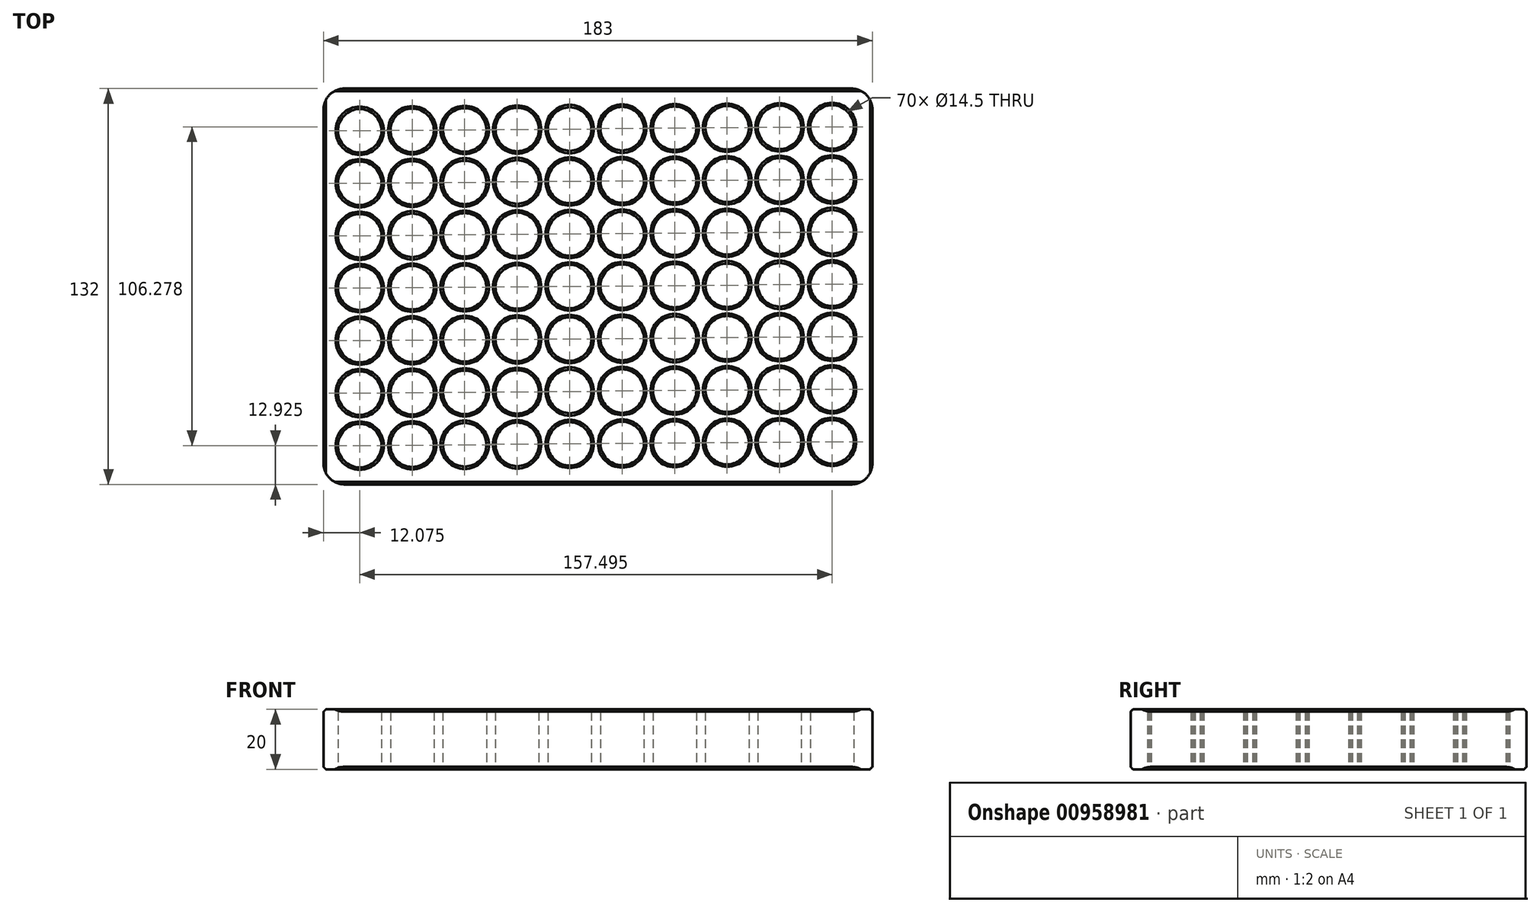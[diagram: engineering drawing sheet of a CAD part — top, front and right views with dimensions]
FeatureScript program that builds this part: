
annotation { "Feature Type Name" : "Feature", "Feature Type Description" : "" }
export const myFeature = defineFeature(function(context is Context, id is Id, definition is map)
    precondition{}
    {
        {
            var Q0;
            Q0=qCreatedBy(makeId("Top.planeOp"),FACE);
            var sketch = newSketch(context, id + "F0", { "sketchPlane" : qUnion([Q0])});
            skCircle(sketch, "E0", {"center": v(-65.97, 12.93) * mm, "radius": 7.25 * mm});
            skCircle(sketch, "E1.0.1.0", {"center": v(-65.97, 30.43) * mm, "radius": 7.25 * mm});
            skCircle(sketch, "E1.1.0.0", {"center": v(-48.47, 13.07) * mm, "radius": 7.25 * mm});
            skCircle(sketch, "E1.1.1.0", {"center": v(-48.47, 30.57) * mm, "radius": 7.25 * mm});
            skLineSegment(sketch, "E1.direction1", {"start": v(-65.97, 12.93) * mm, "end": v(-48.47, 13.07) * mm, "construction": true});
            skLineSegment(sketch, "E1.direction2", {"start": v(-65.97, 12.93) * mm, "end": v(-65.97, 30.43) * mm, "construction": true});
            skLineSegment(sketch, "E2.bottom", {"start": v(-78.04, 132) * mm, "end": v(104.96, 132) * mm});
            skLineSegment(sketch, "E2.top", {"start": v(-78.04, 0) * mm, "end": v(104.96, 0) * mm});
            skLineSegment(sketch, "E2.left", {"start": v(-78.04, 132) * mm, "end": v(-78.04, 0) * mm});
            skLineSegment(sketch, "E2.right", {"start": v(104.96, 132) * mm, "end": v(104.96, 0) * mm});
            skCircle(sketch, "E3.0.0.2", {"center": v(-65.97, 47.93) * mm, "radius": 7.25 * mm});
            skCircle(sketch, "E3.0.0.3", {"center": v(-65.97, 65.43) * mm, "radius": 7.25 * mm});
            skCircle(sketch, "E3.0.0.4", {"center": v(-65.97, 82.93) * mm, "radius": 7.25 * mm});
            skCircle(sketch, "E3.0.0.5", {"center": v(-65.97, 100.43) * mm, "radius": 7.25 * mm});
            skCircle(sketch, "E3.0.0.6", {"center": v(-65.97, 117.93) * mm, "radius": 7.25 * mm});
            skCircle(sketch, "E3.0.1.2", {"center": v(-48.47, 48.07) * mm, "radius": 7.25 * mm});
            skCircle(sketch, "E3.0.1.3", {"center": v(-48.47, 65.57) * mm, "radius": 7.25 * mm});
            skCircle(sketch, "E3.0.1.4", {"center": v(-48.47, 83.07) * mm, "radius": 7.25 * mm});
            skCircle(sketch, "E3.0.1.5", {"center": v(-48.47, 100.57) * mm, "radius": 7.25 * mm});
            skCircle(sketch, "E3.0.1.6", {"center": v(-48.47, 118.07) * mm, "radius": 7.25 * mm});
            skCircle(sketch, "E4.0.2.0", {"center": v(-30.97, 13.2) * mm, "radius": 7.25 * mm});
            skCircle(sketch, "E4.0.2.1", {"center": v(-30.97, 30.7) * mm, "radius": 7.25 * mm});
            skCircle(sketch, "E4.0.2.2", {"center": v(-30.97, 48.2) * mm, "radius": 7.25 * mm});
            skCircle(sketch, "E4.0.2.3", {"center": v(-30.97, 65.7) * mm, "radius": 7.25 * mm});
            skCircle(sketch, "E4.0.2.4", {"center": v(-30.97, 83.2) * mm, "radius": 7.25 * mm});
            skCircle(sketch, "E4.0.2.5", {"center": v(-30.97, 100.7) * mm, "radius": 7.25 * mm});
            skCircle(sketch, "E4.0.2.6", {"center": v(-30.97, 118.2) * mm, "radius": 7.25 * mm});
            skCircle(sketch, "E4.0.3.0", {"center": v(-13.47, 13.35) * mm, "radius": 7.25 * mm});
            skCircle(sketch, "E4.0.3.1", {"center": v(-13.47, 30.85) * mm, "radius": 7.25 * mm});
            skCircle(sketch, "E4.0.3.2", {"center": v(-13.47, 48.35) * mm, "radius": 7.25 * mm});
            skCircle(sketch, "E4.0.3.3", {"center": v(-13.47, 65.85) * mm, "radius": 7.25 * mm});
            skCircle(sketch, "E4.0.3.4", {"center": v(-13.47, 83.35) * mm, "radius": 7.25 * mm});
            skCircle(sketch, "E4.0.3.5", {"center": v(-13.47, 100.85) * mm, "radius": 7.25 * mm});
            skCircle(sketch, "E4.0.3.6", {"center": v(-13.47, 118.35) * mm, "radius": 7.25 * mm});
            skCircle(sketch, "E4.0.4.0", {"center": v(4.03, 13.5) * mm, "radius": 7.25 * mm});
            skCircle(sketch, "E4.0.4.1", {"center": v(4.03, 31) * mm, "radius": 7.25 * mm});
            skCircle(sketch, "E4.0.4.2", {"center": v(4.03, 48.5) * mm, "radius": 7.25 * mm});
            skCircle(sketch, "E4.0.4.3", {"center": v(4.03, 66) * mm, "radius": 7.25 * mm});
            skCircle(sketch, "E4.0.4.4", {"center": v(4.03, 83.5) * mm, "radius": 7.25 * mm});
            skCircle(sketch, "E4.0.4.5", {"center": v(4.03, 101) * mm, "radius": 7.25 * mm});
            skCircle(sketch, "E4.0.4.6", {"center": v(4.03, 118.5) * mm, "radius": 7.25 * mm});
            skCircle(sketch, "E4.0.5.0", {"center": v(21.53, 13.63) * mm, "radius": 7.25 * mm});
            skCircle(sketch, "E4.0.5.1", {"center": v(21.53, 31.13) * mm, "radius": 7.25 * mm});
            skCircle(sketch, "E4.0.5.2", {"center": v(21.53, 48.63) * mm, "radius": 7.25 * mm});
            skCircle(sketch, "E4.0.5.3", {"center": v(21.53, 66.13) * mm, "radius": 7.25 * mm});
            skCircle(sketch, "E4.0.5.4", {"center": v(21.53, 83.63) * mm, "radius": 7.25 * mm});
            skCircle(sketch, "E4.0.5.5", {"center": v(21.53, 101.13) * mm, "radius": 7.25 * mm});
            skCircle(sketch, "E4.0.5.6", {"center": v(21.53, 118.63) * mm, "radius": 7.25 * mm});
            skCircle(sketch, "E4.0.6.0", {"center": v(39.03, 13.78) * mm, "radius": 7.25 * mm});
            skCircle(sketch, "E4.0.6.1", {"center": v(39.03, 31.28) * mm, "radius": 7.25 * mm});
            skCircle(sketch, "E4.0.6.2", {"center": v(39.03, 48.78) * mm, "radius": 7.25 * mm});
            skCircle(sketch, "E4.0.6.3", {"center": v(39.03, 66.28) * mm, "radius": 7.25 * mm});
            skCircle(sketch, "E4.0.6.4", {"center": v(39.03, 83.78) * mm, "radius": 7.25 * mm});
            skCircle(sketch, "E4.0.6.5", {"center": v(39.03, 101.28) * mm, "radius": 7.25 * mm});
            skCircle(sketch, "E4.0.6.6", {"center": v(39.03, 118.78) * mm, "radius": 7.25 * mm});
            skCircle(sketch, "E4.0.7.0", {"center": v(56.53, 13.92) * mm, "radius": 7.25 * mm});
            skCircle(sketch, "E4.0.7.1", {"center": v(56.53, 31.42) * mm, "radius": 7.25 * mm});
            skCircle(sketch, "E4.0.7.2", {"center": v(56.53, 48.92) * mm, "radius": 7.25 * mm});
            skCircle(sketch, "E4.0.7.3", {"center": v(56.53, 66.42) * mm, "radius": 7.25 * mm});
            skCircle(sketch, "E4.0.7.4", {"center": v(56.53, 83.92) * mm, "radius": 7.25 * mm});
            skCircle(sketch, "E4.0.7.5", {"center": v(56.53, 101.42) * mm, "radius": 7.25 * mm});
            skCircle(sketch, "E4.0.7.6", {"center": v(56.53, 118.92) * mm, "radius": 7.25 * mm});
            skCircle(sketch, "E4.0.8.0", {"center": v(74.03, 14.06) * mm, "radius": 7.25 * mm});
            skCircle(sketch, "E4.0.8.1", {"center": v(74.03, 31.56) * mm, "radius": 7.25 * mm});
            skCircle(sketch, "E4.0.8.2", {"center": v(74.03, 49.06) * mm, "radius": 7.25 * mm});
            skCircle(sketch, "E4.0.8.3", {"center": v(74.03, 66.56) * mm, "radius": 7.25 * mm});
            skCircle(sketch, "E4.0.8.4", {"center": v(74.03, 84.06) * mm, "radius": 7.25 * mm});
            skCircle(sketch, "E4.0.8.5", {"center": v(74.03, 101.56) * mm, "radius": 7.25 * mm});
            skCircle(sketch, "E4.0.8.6", {"center": v(74.03, 119.06) * mm, "radius": 7.25 * mm});
            skCircle(sketch, "E4.0.9.0", {"center": v(91.53, 14.2) * mm, "radius": 7.25 * mm});
            skCircle(sketch, "E4.0.9.1", {"center": v(91.53, 31.7) * mm, "radius": 7.25 * mm});
            skCircle(sketch, "E4.0.9.2", {"center": v(91.53, 49.2) * mm, "radius": 7.25 * mm});
            skCircle(sketch, "E4.0.9.3", {"center": v(91.53, 66.7) * mm, "radius": 7.25 * mm});
            skCircle(sketch, "E4.0.9.4", {"center": v(91.53, 84.2) * mm, "radius": 7.25 * mm});
            skCircle(sketch, "E4.0.9.5", {"center": v(91.53, 101.7) * mm, "radius": 7.25 * mm});
            skCircle(sketch, "E4.0.9.6", {"center": v(91.53, 119.2) * mm, "radius": 7.25 * mm});
            skSolve(sketch);
        }
        {
            var Q0;
            Q0=qSketchRegion(id+"F0",true);
            extrude(context, id + "F1", {"entities" : qUnion([Q0]), "depth" : 20 * mm, "offsetDistance" : 25 * mm});
        }
        {
            var Q0;
            Q0=makeQuery(id+"F1.opExtrude","CAP_FACE",FACE,{"disambiguationData":[OSD([sQuery(id+"F0.wireOp",EDGE,"E0"),sQuery(id+"F0.wireOp",EDGE,"E1.0.1.0"),sQuery(id+"F0.wireOp",EDGE,"E1.0.2.0"),sQuery(id+"F0.wireOp",EDGE,"E1.0.3.0"),sQuery(id+"F0.wireOp",EDGE,"E1.0.4.0"),sQuery(id+"F0.wireOp",EDGE,"E1.0.5.0"),sQuery(id+"F0.wireOp",EDGE,"E1.1.0.0"),sQuery(id+"F0.wireOp",EDGE,"E1.1.1.0"),sQuery(id+"F0.wireOp",EDGE,"E1.1.2.0"),sQuery(id+"F0.wireOp",EDGE,"E1.1.3.0"),sQuery(id+"F0.wireOp",EDGE,"E1.1.4.0"),sQuery(id+"F0.wireOp",EDGE,"E1.1.5.0"),sQuery(id+"F0.wireOp",EDGE,"E1.2.0.0"),sQuery(id+"F0.wireOp",EDGE,"E1.2.1.0"),sQuery(id+"F0.wireOp",EDGE,"E1.2.2.0"),sQuery(id+"F0.wireOp",EDGE,"E1.2.3.0"),sQuery(id+"F0.wireOp",EDGE,"E1.2.4.0"),sQuery(id+"F0.wireOp",EDGE,"E1.2.5.0"),sQuery(id+"F0.wireOp",EDGE,"E1.3.0.0"),sQuery(id+"F0.wireOp",EDGE,"E1.3.1.0"),sQuery(id+"F0.wireOp",EDGE,"E1.3.2.0"),sQuery(id+"F0.wireOp",EDGE,"E1.3.3.0"),sQuery(id+"F0.wireOp",EDGE,"E1.3.4.0"),sQuery(id+"F0.wireOp",EDGE,"E1.3.5.0"),sQuery(id+"F0.wireOp",EDGE,"E1.4.0.0"),sQuery(id+"F0.wireOp",EDGE,"E1.4.1.0"),sQuery(id+"F0.wireOp",EDGE,"E1.4.2.0"),sQuery(id+"F0.wireOp",EDGE,"E1.4.3.0"),sQuery(id+"F0.wireOp",EDGE,"E1.4.4.0"),sQuery(id+"F0.wireOp",EDGE,"E1.4.5.0"),sQuery(id+"F0.wireOp",EDGE,"E1.5.0.0"),sQuery(id+"F0.wireOp",EDGE,"E1.5.1.0"),sQuery(id+"F0.wireOp",EDGE,"E1.5.2.0"),sQuery(id+"F0.wireOp",EDGE,"E1.5.3.0"),sQuery(id+"F0.wireOp",EDGE,"E1.5.4.0"),sQuery(id+"F0.wireOp",EDGE,"E1.5.5.0"),sQuery(id+"F0.wireOp",EDGE,"E1.6.0.0"),sQuery(id+"F0.wireOp",EDGE,"E1.6.1.0"),sQuery(id+"F0.wireOp",EDGE,"E1.6.2.0"),sQuery(id+"F0.wireOp",EDGE,"E1.6.3.0"),sQuery(id+"F0.wireOp",EDGE,"E1.6.4.0"),sQuery(id+"F0.wireOp",EDGE,"E1.6.5.0"),sQuery(id+"F0.wireOp",EDGE,"E1.7.0.0"),sQuery(id+"F0.wireOp",EDGE,"E1.7.1.0"),sQuery(id+"F0.wireOp",EDGE,"E1.7.2.0"),sQuery(id+"F0.wireOp",EDGE,"E1.7.3.0"),sQuery(id+"F0.wireOp",EDGE,"E1.7.4.0"),sQuery(id+"F0.wireOp",EDGE,"E1.7.5.0"),sQuery(id+"F0.wireOp",EDGE,"E1.8.0.0"),sQuery(id+"F0.wireOp",EDGE,"E1.8.1.0"),sQuery(id+"F0.wireOp",EDGE,"E1.8.2.0"),sQuery(id+"F0.wireOp",EDGE,"E1.8.3.0"),sQuery(id+"F0.wireOp",EDGE,"E1.8.4.0"),sQuery(id+"F0.wireOp",EDGE,"E1.8.5.0"),sQuery(id+"F0.wireOp",EDGE,"E1.9.0.0"),sQuery(id+"F0.wireOp",EDGE,"E1.9.1.0"),sQuery(id+"F0.wireOp",EDGE,"E1.9.2.0"),sQuery(id+"F0.wireOp",EDGE,"E1.9.3.0"),sQuery(id+"F0.wireOp",EDGE,"E1.9.4.0"),sQuery(id+"F0.wireOp",EDGE,"E1.9.5.0"),sQuery(id+"F0.wireOp",EDGE,"E2.bottom"),sQuery(id+"F0.wireOp",EDGE,"E2.top"),sQuery(id+"F0.wireOp",EDGE,"E2.left"),sQuery(id+"F0.wireOp",EDGE,"E2.right")])],"isStart":false});
            var Q1;
            Q1=makeQuery(id+"F1.opExtrude","CAP_FACE",FACE,{"disambiguationData":[OSD([sQuery(id+"F0.wireOp",EDGE,"E0"),sQuery(id+"F0.wireOp",EDGE,"E1.0.1.0"),sQuery(id+"F0.wireOp",EDGE,"E1.0.2.0"),sQuery(id+"F0.wireOp",EDGE,"E1.0.3.0"),sQuery(id+"F0.wireOp",EDGE,"E1.0.4.0"),sQuery(id+"F0.wireOp",EDGE,"E1.0.5.0"),sQuery(id+"F0.wireOp",EDGE,"E1.1.0.0"),sQuery(id+"F0.wireOp",EDGE,"E1.1.1.0"),sQuery(id+"F0.wireOp",EDGE,"E1.1.2.0"),sQuery(id+"F0.wireOp",EDGE,"E1.1.3.0"),sQuery(id+"F0.wireOp",EDGE,"E1.1.4.0"),sQuery(id+"F0.wireOp",EDGE,"E1.1.5.0"),sQuery(id+"F0.wireOp",EDGE,"E1.2.0.0"),sQuery(id+"F0.wireOp",EDGE,"E1.2.1.0"),sQuery(id+"F0.wireOp",EDGE,"E1.2.2.0"),sQuery(id+"F0.wireOp",EDGE,"E1.2.3.0"),sQuery(id+"F0.wireOp",EDGE,"E1.2.4.0"),sQuery(id+"F0.wireOp",EDGE,"E1.2.5.0"),sQuery(id+"F0.wireOp",EDGE,"E1.3.0.0"),sQuery(id+"F0.wireOp",EDGE,"E1.3.1.0"),sQuery(id+"F0.wireOp",EDGE,"E1.3.2.0"),sQuery(id+"F0.wireOp",EDGE,"E1.3.3.0"),sQuery(id+"F0.wireOp",EDGE,"E1.3.4.0"),sQuery(id+"F0.wireOp",EDGE,"E1.3.5.0"),sQuery(id+"F0.wireOp",EDGE,"E1.4.0.0"),sQuery(id+"F0.wireOp",EDGE,"E1.4.1.0"),sQuery(id+"F0.wireOp",EDGE,"E1.4.2.0"),sQuery(id+"F0.wireOp",EDGE,"E1.4.3.0"),sQuery(id+"F0.wireOp",EDGE,"E1.4.4.0"),sQuery(id+"F0.wireOp",EDGE,"E1.4.5.0"),sQuery(id+"F0.wireOp",EDGE,"E1.5.0.0"),sQuery(id+"F0.wireOp",EDGE,"E1.5.1.0"),sQuery(id+"F0.wireOp",EDGE,"E1.5.2.0"),sQuery(id+"F0.wireOp",EDGE,"E1.5.3.0"),sQuery(id+"F0.wireOp",EDGE,"E1.5.4.0"),sQuery(id+"F0.wireOp",EDGE,"E1.5.5.0"),sQuery(id+"F0.wireOp",EDGE,"E1.6.0.0"),sQuery(id+"F0.wireOp",EDGE,"E1.6.1.0"),sQuery(id+"F0.wireOp",EDGE,"E1.6.2.0"),sQuery(id+"F0.wireOp",EDGE,"E1.6.3.0"),sQuery(id+"F0.wireOp",EDGE,"E1.6.4.0"),sQuery(id+"F0.wireOp",EDGE,"E1.6.5.0"),sQuery(id+"F0.wireOp",EDGE,"E1.7.0.0"),sQuery(id+"F0.wireOp",EDGE,"E1.7.1.0"),sQuery(id+"F0.wireOp",EDGE,"E1.7.2.0"),sQuery(id+"F0.wireOp",EDGE,"E1.7.3.0"),sQuery(id+"F0.wireOp",EDGE,"E1.7.4.0"),sQuery(id+"F0.wireOp",EDGE,"E1.7.5.0"),sQuery(id+"F0.wireOp",EDGE,"E1.8.0.0"),sQuery(id+"F0.wireOp",EDGE,"E1.8.1.0"),sQuery(id+"F0.wireOp",EDGE,"E1.8.2.0"),sQuery(id+"F0.wireOp",EDGE,"E1.8.3.0"),sQuery(id+"F0.wireOp",EDGE,"E1.8.4.0"),sQuery(id+"F0.wireOp",EDGE,"E1.8.5.0"),sQuery(id+"F0.wireOp",EDGE,"E1.9.0.0"),sQuery(id+"F0.wireOp",EDGE,"E1.9.1.0"),sQuery(id+"F0.wireOp",EDGE,"E1.9.2.0"),sQuery(id+"F0.wireOp",EDGE,"E1.9.3.0"),sQuery(id+"F0.wireOp",EDGE,"E1.9.4.0"),sQuery(id+"F0.wireOp",EDGE,"E1.9.5.0"),sQuery(id+"F0.wireOp",EDGE,"E2.bottom"),sQuery(id+"F0.wireOp",EDGE,"E2.top"),sQuery(id+"F0.wireOp",EDGE,"E2.left"),sQuery(id+"F0.wireOp",EDGE,"E2.right")])],"isStart":true});
            chamfer(context, id + "F2", {"entities" : qUnion([Q0, Q1]), "width" : 0.8 * mm, "tangentPropagation" : true});
        }
        {
            var Q0;
            Q0=makeQuery(id+"F1.opExtrude","SWEPT_EDGE",EDGE,{"disambiguationData":[OSD([sQuery(id+"F0.wireOp",EDGE,"E2.top"),sQuery(id+"F0.wireOp",EDGE,"E2.left")])]});
            var Q1;
            Q1=makeQuery(id+"F1.opExtrude","SWEPT_EDGE",EDGE,{"disambiguationData":[OSD([sQuery(id+"F0.wireOp",EDGE,"E2.top"),sQuery(id+"F0.wireOp",EDGE,"E2.right")])]});
            var Q2;
            Q2=makeQuery(id+"F1.opExtrude","SWEPT_EDGE",EDGE,{"disambiguationData":[OSD([sQuery(id+"F0.wireOp",EDGE,"E2.bottom"),sQuery(id+"F0.wireOp",EDGE,"E2.right")])]});
            var Q3;
            Q3=makeQuery(id+"F1.opExtrude","SWEPT_EDGE",EDGE,{"disambiguationData":[OSD([sQuery(id+"F0.wireOp",EDGE,"E2.bottom"),sQuery(id+"F0.wireOp",EDGE,"E2.left")])]});
            fillet(context, id + "F3", {"entities" : qUnion([Q0, Q1, Q2, Q3]), "radius" : 7 * mm, "tangentPropagation" : true, "allowEdgeOverflow" : false});
        }
    });
